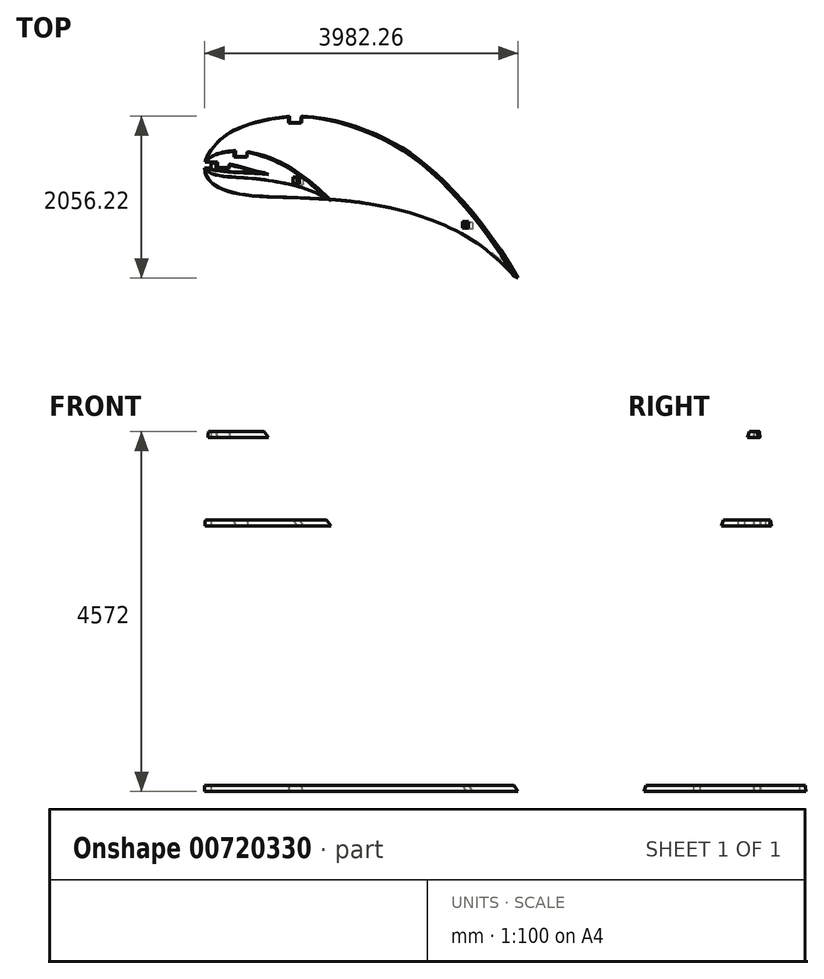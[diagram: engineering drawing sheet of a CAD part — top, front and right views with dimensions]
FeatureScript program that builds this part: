
annotation { "Feature Type Name" : "Feature", "Feature Type Description" : "" }
export const myFeature = defineFeature(function(context is Context, id is Id, definition is map)
    precondition{}
    {
        {
            var Q0;
            Q0=qCreatedBy(makeId("Top.planeOp"),FACE);
            var sketch = newSketch(context, id + "F0", { "sketchPlane" : qUnion([Q0])});
            skLineSegment(sketch, "E0", {"start": v(3981.78, -1434.37) * mm, "end": v(3974.28, -1438.04) * mm});
            skLineSegment(sketch, "E1", {"start": v(85.7, 203.58) * mm, "end": v(135.9, 258.57) * mm});
            skLineSegment(sketch, "E2", {"start": v(135.9, 258.57) * mm, "end": v(200.06, 322.02) * mm});
            skLineSegment(sketch, "E3", {"start": v(200.06, 322.02) * mm, "end": v(244.9, 359.43) * mm});
            skLineSegment(sketch, "E4", {"start": v(244.9, 359.43) * mm, "end": v(305.72, 402.46) * mm});
            skLineSegment(sketch, "E5", {"start": v(305.72, 402.46) * mm, "end": v(355.25, 432.28) * mm});
            skLineSegment(sketch, "E6", {"start": v(355.25, 432.28) * mm, "end": v(436.54, 473.24) * mm});
            skLineSegment(sketch, "E7", {"start": v(436.54, 473.24) * mm, "end": v(505.1, 502.14) * mm});
            skLineSegment(sketch, "E8", {"start": v(505.1, 502.14) * mm, "end": v(547.2, 518.05) * mm});
            skLineSegment(sketch, "E9", {"start": v(547.2, 518.05) * mm, "end": v(645.75, 551) * mm});
            skLineSegment(sketch, "E10", {"start": v(645.75, 551) * mm, "end": v(717.41, 570.86) * mm});
            skLineSegment(sketch, "E11", {"start": v(717.41, 570.86) * mm, "end": v(771.82, 583.4) * mm});
            skLineSegment(sketch, "E12", {"start": v(771.82, 583.4) * mm, "end": v(863.17, 599.45) * mm});
            skLineSegment(sketch, "E13", {"start": v(863.17, 599.45) * mm, "end": v(936.99, 608.65) * mm});
            skLineSegment(sketch, "E14", {"start": v(936.99, 608.65) * mm, "end": v(1020.95, 616.06) * mm});
            skLineSegment(sketch, "E15", {"start": v(1020.95, 616.06) * mm, "end": v(1085.5, 620.05) * mm});
            skLineSegment(sketch, "E16", {"start": v(1085.5, 620.05) * mm, "end": v(1159.87, 622.58) * mm});
            skLineSegment(sketch, "E17", {"start": v(1159.87, 622.58) * mm, "end": v(1234.2, 622.4) * mm});
            skLineSegment(sketch, "E18", {"start": v(1234.2, 622.4) * mm, "end": v(1290.49, 620.15) * mm});
            skLineSegment(sketch, "E19", {"start": v(1290.49, 620.15) * mm, "end": v(1382.4, 612.24) * mm});
            skLineSegment(sketch, "E20", {"start": v(1382.4, 612.24) * mm, "end": v(1456.14, 602.55) * mm});
            skLineSegment(sketch, "E21", {"start": v(1456.14, 602.55) * mm, "end": v(1568.2, 583.4) * mm});
            skLineSegment(sketch, "E22", {"start": v(1568.2, 583.4) * mm, "end": v(1675.53, 561.12) * mm});
            skLineSegment(sketch, "E23", {"start": v(1675.53, 561.12) * mm, "end": v(1747.83, 543.74) * mm});
            skLineSegment(sketch, "E24", {"start": v(1747.83, 543.74) * mm, "end": v(1854.08, 513.96) * mm});
            skLineSegment(sketch, "E25", {"start": v(1854.08, 513.96) * mm, "end": v(1890.59, 502.41) * mm});
            skLineSegment(sketch, "E26", {"start": v(1890.59, 502.41) * mm, "end": v(1960.9, 478.23) * mm});
            skLineSegment(sketch, "E27", {"start": v(1960.9, 478.23) * mm, "end": v(2030.46, 451.9) * mm});
            skLineSegment(sketch, "E28", {"start": v(2030.46, 451.9) * mm, "end": v(2135.88, 407.78) * mm});
            skLineSegment(sketch, "E29", {"start": v(2135.88, 407.78) * mm, "end": v(2301.28, 329.05) * mm});
            skLineSegment(sketch, "E30", {"start": v(2301.28, 329.05) * mm, "end": v(2413.59, 268.92) * mm});
            skLineSegment(sketch, "E31", {"start": v(2413.59, 268.92) * mm, "end": v(2559.73, 181.9) * mm});
            skLineSegment(sketch, "E32", {"start": v(2559.73, 181.9) * mm, "end": v(2621.95, 141.18) * mm});
            skLineSegment(sketch, "E33", {"start": v(2621.95, 141.18) * mm, "end": v(2679.05, 101.48) * mm});
            skLineSegment(sketch, "E34", {"start": v(2679.05, 101.48) * mm, "end": v(2742.61, 54.39) * mm});
            skLineSegment(sketch, "E35", {"start": v(2742.61, 54.39) * mm, "end": v(2801.11, 8.5) * mm});
            skLineSegment(sketch, "E36", {"start": v(2801.11, 8.5) * mm, "end": v(2924.09, -94.55) * mm});
            skLineSegment(sketch, "E37", {"start": v(2924.09, -94.55) * mm, "end": v(3026.4, -185.7) * mm});
            skLineSegment(sketch, "E38", {"start": v(3026.4, -185.7) * mm, "end": v(3152.8, -306.92) * mm});
            skLineSegment(sketch, "E39", {"start": v(3152.8, -306.92) * mm, "end": v(3237.33, -395.2) * mm});
            skLineSegment(sketch, "E40", {"start": v(3237.33, -395.2) * mm, "end": v(3357, -531.54) * mm});
            skLineSegment(sketch, "E41", {"start": v(3357, -531.54) * mm, "end": v(3429.97, -621.6) * mm});
            skLineSegment(sketch, "E42", {"start": v(3429.97, -621.6) * mm, "end": v(3532.6, -756.16) * mm});
            skLineSegment(sketch, "E43", {"start": v(3532.6, -756.16) * mm, "end": v(3608.12, -860.03) * mm});
            skLineSegment(sketch, "E44", {"start": v(3608.12, -860.03) * mm, "end": v(3683.71, -968.53) * mm});
            skLineSegment(sketch, "E45", {"start": v(3683.71, -968.53) * mm, "end": v(3810.32, -1164.56) * mm});
            skLineSegment(sketch, "E46", {"start": v(3810.32, -1164.56) * mm, "end": v(3852.67, -1234.8) * mm});
            skLineSegment(sketch, "E47", {"start": v(3852.67, -1234.8) * mm, "end": v(3904.25, -1315.67) * mm});
            skLineSegment(sketch, "E48", {"start": v(3904.25, -1315.67) * mm, "end": v(3931.4, -1354.4) * mm});
            skLineSegment(sketch, "E49", {"start": v(3931.4, -1354.4) * mm, "end": v(3951.82, -1385.8) * mm});
            skLineSegment(sketch, "E50", {"start": v(3951.82, -1385.8) * mm, "end": v(3965.5, -1409.6) * mm});
            skLineSegment(sketch, "E51", {"start": v(3965.5, -1409.6) * mm, "end": v(3976.53, -1431.19) * mm});
            skLineSegment(sketch, "E52", {"start": v(3976.53, -1431.19) * mm, "end": v(3977.76, -1434.1) * mm});
            skLineSegment(sketch, "E53", {"start": v(3977.76, -1434.1) * mm, "end": v(3977.52, -1436.02) * mm});
            skLineSegment(sketch, "E54", {"start": v(3977.52, -1436.02) * mm, "end": v(3974.68, -1432.88) * mm});
            skLineSegment(sketch, "E55", {"start": v(3974.68, -1432.88) * mm, "end": v(3970.05, -1426.8) * mm});
            skLineSegment(sketch, "E56", {"start": v(3970.05, -1426.8) * mm, "end": v(3963.95, -1418.37) * mm});
            skLineSegment(sketch, "E57", {"start": v(3963.95, -1418.37) * mm, "end": v(3948.7, -1396.74) * mm});
            skLineSegment(sketch, "E58", {"start": v(3948.7, -1396.74) * mm, "end": v(3928.75, -1368.76) * mm});
            skLineSegment(sketch, "E59", {"start": v(3928.75, -1368.76) * mm, "end": v(3899.46, -1330.66) * mm});
            skLineSegment(sketch, "E60", {"start": v(3899.46, -1330.66) * mm, "end": v(3884.92, -1313.42) * mm});
            skLineSegment(sketch, "E61", {"start": v(3884.92, -1313.42) * mm, "end": v(3871.19, -1298.28) * mm});
            skLineSegment(sketch, "E62", {"start": v(3871.19, -1298.28) * mm, "end": v(3858.13, -1284.94) * mm});
            skLineSegment(sketch, "E63", {"start": v(3858.13, -1284.94) * mm, "end": v(3833.49, -1262.37) * mm});
            skLineSegment(sketch, "E64", {"start": v(3833.49, -1262.37) * mm, "end": v(3781.73, -1221.74) * mm});
            skLineSegment(sketch, "E65", {"start": v(3781.73, -1221.74) * mm, "end": v(3761.1, -1205.6) * mm});
            skLineSegment(sketch, "E66", {"start": v(3761.1, -1205.6) * mm, "end": v(3734.78, -1184.46) * mm});
            skLineSegment(sketch, "E67", {"start": v(3734.78, -1184.46) * mm, "end": v(3678.72, -1138.45) * mm});
            skLineSegment(sketch, "E68", {"start": v(3678.72, -1138.45) * mm, "end": v(3619.1, -1089.72) * mm});
            skLineSegment(sketch, "E69", {"start": v(3619.1, -1089.72) * mm, "end": v(3557.15, -1040.93) * mm});
            skLineSegment(sketch, "E70", {"start": v(3557.15, -1040.93) * mm, "end": v(3520.35, -1013.45) * mm});
            skLineSegment(sketch, "E71", {"start": v(3520.35, -1013.45) * mm, "end": v(3430.66, -952.45) * mm});
            skLineSegment(sketch, "E72", {"start": v(3430.66, -952.45) * mm, "end": v(3366.7, -913.62) * mm});
            skLineSegment(sketch, "E73", {"start": v(3366.7, -913.62) * mm, "end": v(3302.14, -877.73) * mm});
            skLineSegment(sketch, "E74", {"start": v(3302.14, -877.73) * mm, "end": v(3236.86, -844.26) * mm});
            skLineSegment(sketch, "E75", {"start": v(3236.86, -844.26) * mm, "end": v(3136.46, -797) * mm});
            skLineSegment(sketch, "E76", {"start": v(3136.46, -797) * mm, "end": v(2967.04, -725.45) * mm});
            skLineSegment(sketch, "E77", {"start": v(2967.04, -725.45) * mm, "end": v(2827.36, -673.38) * mm});
            skLineSegment(sketch, "E78", {"start": v(2827.36, -673.38) * mm, "end": v(2654.54, -617.3) * mm});
            skLineSegment(sketch, "E79", {"start": v(2654.54, -617.3) * mm, "end": v(2542.14, -585.7) * mm});
            skLineSegment(sketch, "E80", {"start": v(2542.14, -585.7) * mm, "end": v(2397.64, -550.34) * mm});
            skLineSegment(sketch, "E81", {"start": v(2397.64, -550.34) * mm, "end": v(2252.1, -520.13) * mm});
            skLineSegment(sketch, "E82", {"start": v(2252.1, -520.13) * mm, "end": v(2131.8, -498.87) * mm});
            skLineSegment(sketch, "E83", {"start": v(2131.8, -498.87) * mm, "end": v(1958.49, -473.58) * mm});
            skLineSegment(sketch, "E84", {"start": v(1958.49, -473.58) * mm, "end": v(1810.72, -456.68) * mm});
            skLineSegment(sketch, "E85", {"start": v(1810.72, -456.68) * mm, "end": v(1633.55, -441.7) * mm});
            skLineSegment(sketch, "E86", {"start": v(1633.55, -441.7) * mm, "end": v(1514.16, -434.54) * mm});
            skLineSegment(sketch, "E87", {"start": v(1514.16, -434.54) * mm, "end": v(1365.64, -427.92) * mm});
            skLineSegment(sketch, "E88", {"start": v(1365.64, -427.92) * mm, "end": v(1184.3, -421.27) * mm});
            skLineSegment(sketch, "E89", {"start": v(1184.3, -421.27) * mm, "end": v(808.58, -404.94) * mm});
            skLineSegment(sketch, "E90", {"start": v(808.58, -404.94) * mm, "end": v(623.2, -392.8) * mm});
            skLineSegment(sketch, "E91", {"start": v(623.2, -392.8) * mm, "end": v(549.21, -385.3) * mm});
            skLineSegment(sketch, "E92", {"start": v(549.21, -385.3) * mm, "end": v(510.45, -380.43) * mm});
            skLineSegment(sketch, "E93", {"start": v(510.45, -380.43) * mm, "end": v(402.1, -362.18) * mm});
            skLineSegment(sketch, "E94", {"start": v(402.1, -362.18) * mm, "end": v(329.77, -344.76) * mm});
            skLineSegment(sketch, "E95", {"start": v(329.77, -344.76) * mm, "end": v(285.83, -331.42) * mm});
            skLineSegment(sketch, "E96", {"start": v(285.83, -331.42) * mm, "end": v(224.46, -308.34) * mm});
            skLineSegment(sketch, "E97", {"start": v(224.46, -308.34) * mm, "end": v(190.7, -292.72) * mm});
            skLineSegment(sketch, "E98", {"start": v(190.7, -292.72) * mm, "end": v(157.86, -274.98) * mm});
            skLineSegment(sketch, "E99", {"start": v(157.86, -274.98) * mm, "end": v(130.63, -257.91) * mm});
            skLineSegment(sketch, "E100", {"start": v(130.63, -257.91) * mm, "end": v(95.96, -232.16) * mm});
            skLineSegment(sketch, "E101", {"start": v(95.96, -232.16) * mm, "end": v(68.35, -206.64) * mm});
            skLineSegment(sketch, "E102", {"start": v(68.35, -206.64) * mm, "end": v(44.44, -178.1) * mm});
            skLineSegment(sketch, "E103", {"start": v(44.44, -178.1) * mm, "end": v(32.62, -159.9) * mm});
            skLineSegment(sketch, "E104", {"start": v(32.62, -159.9) * mm, "end": v(11.66, -111.7) * mm});
            skLineSegment(sketch, "E105", {"start": v(11.66, -111.7) * mm, "end": v(3.04, -75.1) * mm});
            skLineSegment(sketch, "E106", {"start": v(3.04, -75.1) * mm, "end": v(-0.05, -49.63) * mm});
            skLineSegment(sketch, "E107", {"start": v(-0.05, -49.63) * mm, "end": v(0, 0) * mm});
            skLineSegment(sketch, "E108", {"start": v(0, 0) * mm, "end": v(5.25, 37.05) * mm});
            skLineSegment(sketch, "E109", {"start": v(5.25, 37.05) * mm, "end": v(16.28, 76.98) * mm});
            skLineSegment(sketch, "E110", {"start": v(16.28, 76.98) * mm, "end": v(28.73, 107.24) * mm});
            skLineSegment(sketch, "E111", {"start": v(28.73, 107.24) * mm, "end": v(45.88, 140.13) * mm});
            skLineSegment(sketch, "E112", {"start": v(45.88, 140.13) * mm, "end": v(85.7, 203.58) * mm});
            skSolve(sketch);
        }
        {
            var Q0;
            Q0=qCreatedBy(makeId("Top.planeOp"),FACE);
            var sketch = newSketch(context, id + "F1", { "sketchPlane" : qUnion([Q0])});
            skPoint(sketch, "E113", {"position": v(0, 0) * mm});
            skPoint(sketch, "E114.0", {"position": v(-0.05, -49.63) * mm});
            skPoint(sketch, "E114.1", {"position": v(11.66, -111.7) * mm});
            skPoint(sketch, "E114.2", {"position": v(68.35, -206.64) * mm});
            skPoint(sketch, "E114.3", {"position": v(5.25, 37.05) * mm});
            skPoint(sketch, "E114.4", {"position": v(28.73, 107.24) * mm});
            skPoint(sketch, "E114.5", {"position": v(135.9, 258.57) * mm});
            skPoint(sketch, "E114.6", {"position": v(355.25, 432.28) * mm});
            skPoint(sketch, "E114.7", {"position": v(1159.87, 622.58) * mm});
            skPoint(sketch, "E114.8", {"position": v(2135.88, 407.78) * mm});
            skPoint(sketch, "E114.9", {"position": v(3981.78, -1434.37) * mm});
            skPoint(sketch, "E114.10", {"position": v(2967.04, -725.45) * mm});
            skPoint(sketch, "E114.11", {"position": v(1810.72, -456.68) * mm});
            skPoint(sketch, "E114.12", {"position": v(808.58, -404.94) * mm});
            skPoint(sketch, "E114.13", {"position": v(285.83, -331.42) * mm});
            skPoint(sketch, "E114.14", {"position": v(2862.6, -43.02) * mm});
            skFitSpline(sketch, "E115", {"points": [v(0, 0) * mm, v(-0.05, -49.63) * mm, v(11.66, -111.7) * mm, v(68.35, -206.64) * mm, v(285.83, -331.42) * mm, v(808.58, -404.94) * mm, v(1810.72, -456.68) * mm, v(2967.04, -725.45) * mm, v(3981.78, -1434.37) * mm], "startDerivative": vector(-39.2, -1147.22) * mm, "endDerivative": vector(4484.15, -5091.63) * mm});
            skFitSpline(sketch, "E116", {"points": [v(0, 0) * mm, v(5.25, 37.05) * mm, v(28.73, 107.24) * mm, v(135.9, 258.57) * mm, v(355.25, 432.28) * mm, v(1159.87, 622.58) * mm, v(2135.88, 407.78) * mm, v(2862.6, -43.02) * mm, v(3981.78, -1434.37) * mm], "startDerivative": vector(115.79, 1014.55) * mm, "endDerivative": vector(4272.99, -7495.32) * mm});
            skSolve(sketch);
        }
        {
            var Q0;
            Q0=qCreatedBy(makeId("Top.planeOp"),FACE);
            cPlane(context, id + "F2", {"entities" : qUnion([Q0]), "cplaneType" : CPlaneType.OFFSET, "offset" : 4572 * mm, "width" : 152.4 * mm, "height" : 152.4 * mm});
        }
        {
            var Q0;
            Q0=qCreatedBy(id+"F2.planeOp",FACE);
            var sketch = newSketch(context, id + "F3", { "sketchPlane" : qUnion([Q0])});
            skLineSegment(sketch, "E117", {"start": v(0, 0) * mm, "end": v(2.44, 5.76) * mm});
            skLineSegment(sketch, "E118", {"start": v(2.44, 5.76) * mm, "end": v(3.9, 8.43) * mm});
            skLineSegment(sketch, "E119", {"start": v(3.9, 8.43) * mm, "end": v(6.05, 11.35) * mm});
            skLineSegment(sketch, "E120", {"start": v(6.05, 11.35) * mm, "end": v(7.68, 12.92) * mm});
            skLineSegment(sketch, "E121", {"start": v(7.68, 12.92) * mm, "end": v(10.08, 14.68) * mm});
            skLineSegment(sketch, "E122", {"start": v(10.08, 14.68) * mm, "end": v(15.58, 17.45) * mm});
            skLineSegment(sketch, "E123", {"start": v(15.58, 17.45) * mm, "end": v(21.94, 19.67) * mm});
            skLineSegment(sketch, "E124", {"start": v(21.94, 19.67) * mm, "end": v(39.32, 24.27) * mm});
            skLineSegment(sketch, "E125", {"start": v(39.32, 24.27) * mm, "end": v(46.9, 25.72) * mm});
            skLineSegment(sketch, "E126", {"start": v(46.9, 25.72) * mm, "end": v(63.21, 27.76) * mm});
            skLineSegment(sketch, "E127", {"start": v(63.21, 27.76) * mm, "end": v(80.93, 28.74) * mm});
            skLineSegment(sketch, "E128", {"start": v(80.93, 28.74) * mm, "end": v(87.62, 28.87) * mm});
            skLineSegment(sketch, "E129", {"start": v(87.62, 28.87) * mm, "end": v(123.3, 27.99) * mm});
            skLineSegment(sketch, "E130", {"start": v(123.3, 27.99) * mm, "end": v(136.22, 27.24) * mm});
            skLineSegment(sketch, "E131", {"start": v(136.22, 27.24) * mm, "end": v(172.46, 24.2) * mm});
            skLineSegment(sketch, "E132", {"start": v(172.46, 24.2) * mm, "end": v(184.68, 22.84) * mm});
            skLineSegment(sketch, "E133", {"start": v(184.68, 22.84) * mm, "end": v(208.8, 19.63) * mm});
            skLineSegment(sketch, "E134", {"start": v(208.8, 19.63) * mm, "end": v(227.68, 16.64) * mm});
            skLineSegment(sketch, "E135", {"start": v(227.68, 16.64) * mm, "end": v(287.43, 5.3) * mm});
            skLineSegment(sketch, "E136", {"start": v(287.43, 5.3) * mm, "end": v(328.35, -2.8) * mm});
            skLineSegment(sketch, "E137", {"start": v(328.35, -2.8) * mm, "end": v(350.97, -7.56) * mm});
            skLineSegment(sketch, "E138", {"start": v(350.97, -7.56) * mm, "end": v(375.86, -13.24) * mm});
            skLineSegment(sketch, "E139", {"start": v(375.86, -13.24) * mm, "end": v(415.26, -22.7) * mm});
            skLineSegment(sketch, "E140", {"start": v(415.26, -22.7) * mm, "end": v(480.32, -37.82) * mm});
            skLineSegment(sketch, "E141", {"start": v(480.32, -37.82) * mm, "end": v(518.03, -46.34) * mm});
            skLineSegment(sketch, "E142", {"start": v(518.03, -46.34) * mm, "end": v(543.1, -52.2) * mm});
            skLineSegment(sketch, "E143", {"start": v(543.1, -52.2) * mm, "end": v(601.34, -66.56) * mm});
            skLineSegment(sketch, "E144", {"start": v(601.34, -66.56) * mm, "end": v(636.38, -74.84) * mm});
            skLineSegment(sketch, "E145", {"start": v(636.38, -74.84) * mm, "end": v(653.53, -78.67) * mm});
            skLineSegment(sketch, "E146", {"start": v(653.53, -78.67) * mm, "end": v(683.57, -85.02) * mm});
            skLineSegment(sketch, "E147", {"start": v(683.57, -85.02) * mm, "end": v(696.65, -87.74) * mm});
            skLineSegment(sketch, "E148", {"start": v(696.65, -87.74) * mm, "end": v(720.28, -92.43) * mm});
            skLineSegment(sketch, "E149", {"start": v(720.28, -92.43) * mm, "end": v(725.98, -93.35) * mm});
            skLineSegment(sketch, "E150", {"start": v(725.98, -93.35) * mm, "end": v(729.17, -93.8) * mm});
            skLineSegment(sketch, "E151", {"start": v(729.17, -93.8) * mm, "end": v(736.55, -94.66) * mm});
            skLineSegment(sketch, "E152", {"start": v(736.55, -94.66) * mm, "end": v(742.43, -95.48) * mm});
            skLineSegment(sketch, "E153", {"start": v(742.43, -95.48) * mm, "end": v(745.85, -96.07) * mm});
            skLineSegment(sketch, "E154", {"start": v(745.85, -96.07) * mm, "end": v(749.6, -96.82) * mm});
            skLineSegment(sketch, "E155", {"start": v(749.6, -96.82) * mm, "end": v(753.66, -97.74) * mm});
            skLineSegment(sketch, "E156", {"start": v(753.66, -97.74) * mm, "end": v(755.05, -98.1) * mm});
            skLineSegment(sketch, "E157", {"start": v(755.05, -98.1) * mm, "end": v(755.65, -98.33) * mm});
            skLineSegment(sketch, "E158", {"start": v(755.65, -98.33) * mm, "end": v(755.22, -98.36) * mm});
            skLineSegment(sketch, "E159", {"start": v(755.22, -98.36) * mm, "end": v(753.96, -98.24) * mm});
            skLineSegment(sketch, "E160", {"start": v(753.96, -98.24) * mm, "end": v(748.84, -97.58) * mm});
            skLineSegment(sketch, "E161", {"start": v(748.84, -97.58) * mm, "end": v(745.9, -97.19) * mm});
            skLineSegment(sketch, "E162", {"start": v(745.9, -97.19) * mm, "end": v(742.3, -96.73) * mm});
            skLineSegment(sketch, "E163", {"start": v(742.3, -96.73) * mm, "end": v(739.1, -96.35) * mm});
            skLineSegment(sketch, "E164", {"start": v(739.1, -96.35) * mm, "end": v(736.2, -96.03) * mm});
            skLineSegment(sketch, "E165", {"start": v(736.2, -96.03) * mm, "end": v(730.95, -95.55) * mm});
            skLineSegment(sketch, "E166", {"start": v(730.95, -95.55) * mm, "end": v(727.66, -95.3) * mm});
            skLineSegment(sketch, "E167", {"start": v(727.66, -95.3) * mm, "end": v(720.08, -94.85) * mm});
            skLineSegment(sketch, "E168", {"start": v(720.08, -94.85) * mm, "end": v(707.85, -94.3) * mm});
            skLineSegment(sketch, "E169", {"start": v(707.85, -94.3) * mm, "end": v(694.38, -93.8) * mm});
            skLineSegment(sketch, "E170", {"start": v(694.38, -93.8) * mm, "end": v(649.75, -92.28) * mm});
            skLineSegment(sketch, "E171", {"start": v(649.75, -92.28) * mm, "end": v(596.8, -90.77) * mm});
            skLineSegment(sketch, "E172", {"start": v(596.8, -90.77) * mm, "end": v(537.05, -90.01) * mm});
            skLineSegment(sketch, "E173", {"start": v(537.05, -90.01) * mm, "end": v(512.7, -89.51) * mm});
            skLineSegment(sketch, "E174", {"start": v(512.7, -89.51) * mm, "end": v(472.75, -88.5) * mm});
            skLineSegment(sketch, "E175", {"start": v(472.75, -88.5) * mm, "end": v(406.19, -86.99) * mm});
            skLineSegment(sketch, "E176", {"start": v(406.19, -86.99) * mm, "end": v(366.78, -85.77) * mm});
            skLineSegment(sketch, "E177", {"start": v(366.78, -85.77) * mm, "end": v(341.14, -84.72) * mm});
            skLineSegment(sketch, "E178", {"start": v(341.14, -84.72) * mm, "end": v(276.84, -80.93) * mm});
            skLineSegment(sketch, "E179", {"start": v(276.84, -80.93) * mm, "end": v(245.36, -78.48) * mm});
            skLineSegment(sketch, "E180", {"start": v(245.36, -78.48) * mm, "end": v(216.33, -75.64) * mm});
            skLineSegment(sketch, "E181", {"start": v(216.33, -75.64) * mm, "end": v(196.98, -73.34) * mm});
            skLineSegment(sketch, "E182", {"start": v(196.98, -73.34) * mm, "end": v(161.11, -68.08) * mm});
            skLineSegment(sketch, "E183", {"start": v(161.11, -68.08) * mm, "end": v(148.89, -65.97) * mm});
            skLineSegment(sketch, "E184", {"start": v(148.89, -65.97) * mm, "end": v(124.98, -61.47) * mm});
            skLineSegment(sketch, "E185", {"start": v(124.98, -61.47) * mm, "end": v(112.7, -59) * mm});
            skLineSegment(sketch, "E186", {"start": v(112.7, -59) * mm, "end": v(89.3, -53.87) * mm});
            skLineSegment(sketch, "E187", {"start": v(89.3, -53.87) * mm, "end": v(71.86, -49.17) * mm});
            skLineSegment(sketch, "E188", {"start": v(71.86, -49.17) * mm, "end": v(65.84, -47.26) * mm});
            skLineSegment(sketch, "E189", {"start": v(65.84, -47.26) * mm, "end": v(54.33, -43.15) * mm});
            skLineSegment(sketch, "E190", {"start": v(54.33, -43.15) * mm, "end": v(40.09, -37.06) * mm});
            skLineSegment(sketch, "E191", {"start": v(40.09, -37.06) * mm, "end": v(32.34, -33.2) * mm});
            skLineSegment(sketch, "E192", {"start": v(32.34, -33.2) * mm, "end": v(16.64, -24.2) * mm});
            skLineSegment(sketch, "E193", {"start": v(16.64, -24.2) * mm, "end": v(11.09, -20.57) * mm});
            skLineSegment(sketch, "E194", {"start": v(11.09, -20.57) * mm, "end": v(6.37, -16.6) * mm});
            skLineSegment(sketch, "E195", {"start": v(6.37, -16.6) * mm, "end": v(4.43, -14.33) * mm});
            skLineSegment(sketch, "E196", {"start": v(4.43, -14.33) * mm, "end": v(3.03, -12.1) * mm});
            skLineSegment(sketch, "E197", {"start": v(3.03, -12.1) * mm, "end": v(1.77, -9.1) * mm});
            skLineSegment(sketch, "E198", {"start": v(1.77, -9.1) * mm, "end": v(1, -6.17) * mm});
            skLineSegment(sketch, "E199", {"start": v(1, -6.17) * mm, "end": v(0, 0) * mm});
            skSolve(sketch);
        }
        {
            var Q0;
            Q0=qCreatedBy(id+"F2.planeOp",FACE);
            var sketch = newSketch(context, id + "F4", { "sketchPlane" : qUnion([Q0])});
            skPoint(sketch, "E200.0", {"position": v(2.44, 5.76) * mm});
            skPoint(sketch, "E201.0", {"position": v(0, 0) * mm});
            skPoint(sketch, "E202.0", {"position": v(1, -6.17) * mm});
            skPoint(sketch, "E203.0", {"position": v(5.4, -15.46) * mm});
            skPoint(sketch, "E204.0", {"position": v(16.64, -24.2) * mm});
            skPoint(sketch, "E205.0", {"position": v(40.09, -37.06) * mm});
            skPoint(sketch, "E206.0", {"position": v(89.3, -53.87) * mm});
            skPoint(sketch, "E207.0", {"position": v(148.89, -65.97) * mm});
            skPoint(sketch, "E207.1", {"position": v(341.14, -84.72) * mm});
            skPoint(sketch, "E207.2", {"position": v(755.65, -98.33) * mm});
            skPoint(sketch, "E207.3", {"position": v(415.26, -22.7) * mm});
            skPoint(sketch, "E207.4", {"position": v(227.68, 16.64) * mm});
            skPoint(sketch, "E207.5", {"position": v(80.93, 28.74) * mm});
            skPoint(sketch, "E207.6", {"position": v(39.32, 24.27) * mm});
            skPoint(sketch, "E207.7", {"position": v(15.58, 17.45) * mm});
            skPoint(sketch, "E207.8", {"position": v(6.87, 12.13) * mm});
            skFitSpline(sketch, "E208", {"points": [v(0, 0) * mm, v(2.44, 5.76) * mm, v(6.87, 12.13) * mm, v(15.58, 17.45) * mm, v(39.32, 24.27) * mm, v(80.93, 28.74) * mm, v(227.68, 16.64) * mm, v(415.26, -22.7) * mm, v(755.65, -98.33) * mm], "startDerivative": vector(56.06, 146.59) * mm, "endDerivative": vector(1282.77, -261.85) * mm});
            skFitSpline(sketch, "E209", {"points": [v(0, 0) * mm, v(1, -6.17) * mm, v(5.4, -15.46) * mm, v(16.64, -24.2) * mm, v(40.09, -37.06) * mm, v(89.3, -53.87) * mm, v(148.89, -65.97) * mm, v(341.14, -84.72) * mm, v(755.65, -98.33) * mm], "startDerivative": vector(15.7, -149.12) * mm, "endDerivative": vector(1341.07, -77.84) * mm});
            skSolve(sketch);
        }
        {
            var Q0;
            Q0=makeQuery(id+"F1.imprint","IMPRINT",FACE,{"disambiguationData":[TD([[makeQuery(id+"F1.imprint","IMPRINT",EDGE,{"derivedFrom":sQuery(id+"F1.wireOp",EDGE,"E115")}),1.0]])]});
            var Q1;
            Q1=makeQuery(id+"F4.imprint","IMPRINT",FACE,{"disambiguationData":[TD([[makeQuery(id+"F4.imprint","IMPRINT",EDGE,{"derivedFrom":sQuery(id+"F4.wireOp",EDGE,"E208")}),-1.0]])]});
            loft(context, id + "F5", {"sheetProfilesArray" : [{ "sheetProfileEntities" : qUnion([Q0]) }, { "sheetProfileEntities" : qUnion([Q1]) }]});
        }
        {
            var Q0;
            Q0=qCreatedBy(makeId("Front.planeOp"),FACE);
            var sketch = newSketch(context, id + "F6", { "sketchPlane" : qUnion([Q0])});
            skPoint(sketch, "E210", {"position": v(0, 0) * mm});
            skLineSegment(sketch, "E211", {"start": v(0, 0) * mm, "end": v(0, 76.2) * mm, "construction": true});
            skLineSegment(sketch, "E212.bottom", {"start": v(0, 76.2) * mm, "end": v(5797.2, 76.2) * mm});
            skLineSegment(sketch, "E212.top", {"start": v(0, 1123.95) * mm, "end": v(5797.2, 1123.95) * mm});
            skLineSegment(sketch, "E212.left", {"start": v(0, 76.2) * mm, "end": v(0, 1123.95) * mm});
            skLineSegment(sketch, "E212.right", {"start": v(5797.2, 76.2) * mm, "end": v(5797.2, 1123.95) * mm});
            skLineSegment(sketch, "E213.0.1.0", {"start": v(0, 1200.15) * mm, "end": v(5797.2, 1200.15) * mm});
            skLineSegment(sketch, "E213.0.1.1", {"start": v(0, 2247.9) * mm, "end": v(5797.2, 2247.9) * mm});
            skLineSegment(sketch, "E213.0.1.2", {"start": v(0, 1200.15) * mm, "end": v(0, 2247.9) * mm});
            skLineSegment(sketch, "E213.0.1.3", {"start": v(5797.2, 1200.15) * mm, "end": v(5797.2, 2247.9) * mm});
            skPoint(sketch, "E213.0.1.4", {"position": v(0, 1123.95) * mm});
            skLineSegment(sketch, "E213.0.1.5", {"start": v(0, 1123.95) * mm, "end": v(0, 1200.15) * mm, "construction": true});
            skLineSegment(sketch, "E213.0.2.0", {"start": v(0, 2324.1) * mm, "end": v(5797.2, 2324.1) * mm});
            skLineSegment(sketch, "E213.0.2.1", {"start": v(0, 3371.85) * mm, "end": v(5797.2, 3371.85) * mm});
            skLineSegment(sketch, "E213.0.2.2", {"start": v(0, 2324.1) * mm, "end": v(0, 3371.85) * mm});
            skLineSegment(sketch, "E213.0.2.3", {"start": v(5797.2, 2324.1) * mm, "end": v(5797.2, 3371.85) * mm});
            skPoint(sketch, "E213.0.2.4", {"position": v(0, 2247.9) * mm});
            skLineSegment(sketch, "E213.0.2.5", {"start": v(0, 2247.9) * mm, "end": v(0, 2324.1) * mm, "construction": true});
            skLineSegment(sketch, "E213.0.3.0", {"start": v(0, 3448.05) * mm, "end": v(5797.2, 3448.05) * mm});
            skLineSegment(sketch, "E213.0.3.1", {"start": v(0, 4495.8) * mm, "end": v(5797.2, 4495.8) * mm});
            skLineSegment(sketch, "E213.0.3.2", {"start": v(0, 3448.05) * mm, "end": v(0, 4495.8) * mm});
            skLineSegment(sketch, "E213.0.3.3", {"start": v(5797.2, 3448.05) * mm, "end": v(5797.2, 4495.8) * mm});
            skPoint(sketch, "E213.0.3.4", {"position": v(0, 3371.85) * mm});
            skLineSegment(sketch, "E213.0.3.5", {"start": v(0, 3371.85) * mm, "end": v(0, 3448.05) * mm, "construction": true});
            skLineSegment(sketch, "E213.direction1", {"start": v(0, 0) * mm, "end": v(25.4, 0) * mm, "construction": true});
            skLineSegment(sketch, "E213.direction2", {"start": v(0, 0) * mm, "end": v(0, 1123.95) * mm, "construction": true});
            skSolve(sketch);
        }
        {
            var Q0;
            Q0=makeQuery(id+"F6.imprint","IMPRINT",FACE,{"disambiguationData":[TD([[makeQuery(id+"F6.imprint","IMPRINT",EDGE,{"derivedFrom":sQuery(id+"F6.wireOp",EDGE,"E213.0.3.0")}),1.0]])]});
            var Q1;
            Q1=makeQuery(id+"F6.imprint","IMPRINT",FACE,{"disambiguationData":[TD([[makeQuery(id+"F6.imprint","IMPRINT",EDGE,{"derivedFrom":sQuery(id+"F6.wireOp",EDGE,"E213.0.2.0")}),1.0]])]});
            var Q2;
            Q2=makeQuery(id+"F6.imprint","IMPRINT",FACE,{"disambiguationData":[TD([[makeQuery(id+"F6.imprint","IMPRINT",EDGE,{"derivedFrom":sQuery(id+"F6.wireOp",EDGE,"E213.0.1.0")}),1.0]])]});
            var Q3;
            Q3=makeQuery(id+"F6.imprint","IMPRINT",FACE,{"disambiguationData":[TD([[makeQuery(id+"F6.imprint","IMPRINT",EDGE,{"derivedFrom":sQuery(id+"F6.wireOp",EDGE,"E212.bottom")}),1.0]])]});
            extrude(context, id + "F7", {"entities" : qUnion([Q0, Q1, Q2, Q3]), "operationType" : NewBodyOperationType.REMOVE, "endBound" : BoundingType.SYMMETRIC, "oppositeDirection" : true, "depth" : 3556 * mm, "offsetDistance" : 25.4 * mm});
        }
        {
            var Q0;
            Q0=makeQuery(id+"F7.boolean.opBoolean","COPY",FACE,{"derivedFrom":makeQuery(id+"F7.opExtrude","SWEPT_FACE",FACE,{"disambiguationData":[OSD([sQuery(id+"F6.wireOp",EDGE,"E212.left")])]})});
            var Q1;
            Q1=makeQuery(id+"F7.boolean.opBoolean","COPY",FACE,{"derivedFrom":makeQuery(id+"F7.opExtrude","SWEPT_FACE",FACE,{"disambiguationData":[OSD([sQuery(id+"F6.wireOp",EDGE,"E213.0.1.2")])]})});
            var Q2;
            Q2=makeQuery(id+"F7.boolean.opBoolean","COPY",FACE,{"derivedFrom":makeQuery(id+"F7.opExtrude","SWEPT_FACE",FACE,{"disambiguationData":[OSD([sQuery(id+"F6.wireOp",EDGE,"E213.0.2.2")])]})});
            extrude(context, id + "F8", {"entities" : qUnion([Q0, Q1, Q2]), "operationType" : NewBodyOperationType.REMOVE, "oppositeDirection" : true, "depth" : 127 * mm, "offsetDistance" : 25.4 * mm});
        }
        {
            var Q0;
            Q0=qCreatedBy(makeId("Top.planeOp"),FACE);
            var sketch = newSketch(context, id + "F9", { "sketchPlane" : qUnion([Q0])});
            skPoint(sketch, "E214", {"position": v(0, 0) * mm});
            skLineSegment(sketch, "E215", {"start": v(0, 0) * mm, "end": v(80.65, 0) * mm, "construction": true});
            skLineSegment(sketch, "E216", {"start": v(80.65, 0) * mm, "end": v(80.65, 40.34) * mm});
            skLineSegment(sketch, "E217", {"start": v(80.65, 0) * mm, "end": v(80.65, -40.34) * mm});
            skLineSegment(sketch, "E218", {"start": v(80.65, -40.34) * mm, "end": v(0, -40.34) * mm});
            skLineSegment(sketch, "E219", {"start": v(80.65, 40.34) * mm, "end": v(0, 40.34) * mm});
            skLineSegment(sketch, "E220", {"start": v(0, 40.34) * mm, "end": v(0, -40.34) * mm});
            skSolve(sketch);
        }
        {
            var Q0;
            Q0=makeQuery(id+"F9.imprint","IMPRINT",FACE,{"disambiguationData":[TD([[makeQuery(id+"F9.imprint","IMPRINT",EDGE,{"derivedFrom":sQuery(id+"F9.wireOp",EDGE,"E216")}),1.0]])]});
            extrude(context, id + "F10", {"entities" : qUnion([Q0]), "operationType" : NewBodyOperationType.REMOVE, "depth" : 5080 * mm, "offsetDistance" : 25.4 * mm});
        }
        {
            var Q0;
            Q0=makeQuery(id+"F10.boolean.opBoolean","SPLIT",BODY,{"disambiguationData":[OD(0.0)],"derivedFrom":makeQuery(id+"F8.boolean.opBoolean","SPLIT",BODY,{"disambiguationData":[OD(1.0)],"derivedFrom":makeQuery(id+"F7.boolean.opBoolean","SPLIT",BODY,{"disambiguationData":[OD(2.0)],"derivedFrom":makeQuery(id+"F5.opLoft","SWEPT_BODY",BODY,{"disambiguationData":[OSD([makeQuery(id+"F1.imprint","IMPRINT",FACE,{"disambiguationData":[TD([[makeQuery(id+"F1.imprint","IMPRINT",EDGE,{"derivedFrom":sQuery(id+"F1.wireOp",EDGE,"E115")}),1.0]])]}),makeQuery(id+"F4.imprint","IMPRINT",FACE,{"disambiguationData":[TD([[makeQuery(id+"F4.imprint","IMPRINT",EDGE,{"derivedFrom":sQuery(id+"F4.wireOp",EDGE,"E208")}),-1.0]])]})])]})})})});
            var Q1;
            Q1=makeQuery(id+"F10.boolean.opBoolean","SPLIT",BODY,{"disambiguationData":[OD(0.0)],"derivedFrom":makeQuery(id+"F8.boolean.opBoolean","SPLIT",BODY,{"disambiguationData":[OD(2.0)],"derivedFrom":makeQuery(id+"F7.boolean.opBoolean","SPLIT",BODY,{"disambiguationData":[OD(2.0)],"derivedFrom":makeQuery(id+"F5.opLoft","SWEPT_BODY",BODY,{"disambiguationData":[OSD([makeQuery(id+"F1.imprint","IMPRINT",FACE,{"disambiguationData":[TD([[makeQuery(id+"F1.imprint","IMPRINT",EDGE,{"derivedFrom":sQuery(id+"F1.wireOp",EDGE,"E115")}),1.0]])]}),makeQuery(id+"F4.imprint","IMPRINT",FACE,{"disambiguationData":[TD([[makeQuery(id+"F4.imprint","IMPRINT",EDGE,{"derivedFrom":sQuery(id+"F4.wireOp",EDGE,"E208")}),-1.0]])]})])]})})})});
            deleteBodies(context, id + "F11", {"entities" : qUnion([Q0, Q1])});
        }
        {
            var Q0;
            {var subQ0=sQuery(id+"F6.wireOp",EDGE,"E212.bottom");Q0=makeQuery(id+"F10.boolean.opBoolean","COPY",FACE,{"disambiguationData":[TD([makeQuery(id+"F7.boolean.opBoolean","COPY",FACE,{"derivedFrom":makeQuery(id+"F7.opExtrude","SWEPT_FACE",FACE,{"disambiguationData":[OSD([subQ0])]})})])],"derivedFrom":makeQuery(id+"F10.opExtrude","SWEPT_FACE",FACE,{"disambiguationData":[OSD([sQuery(id+"F9.wireOp",EDGE,"E220")])]})});}
            extrude(context, id + "F12", {"entities" : qUnion([Q0]), "operationType" : NewBodyOperationType.REMOVE, "oppositeDirection" : true, "depth" : 25.4 * mm, "offsetDistance" : 25.4 * mm});
        }
        {
            var Q0;
            Q0=makeQuery(id+"F1.imprint","IMPRINT",FACE,{"disambiguationData":[TD([[makeQuery(id+"F1.imprint","IMPRINT",EDGE,{"derivedFrom":sQuery(id+"F1.wireOp",EDGE,"E115")}),1.0]])]});
            var sketch = newSketch(context, id + "F13", { "sketchPlane" : qUnion([Q0])});
            skPoint(sketch, "E221.0", {"position": v(1159.87, 622.58) * mm});
            skLineSegment(sketch, "E222", {"start": v(1159.87, 622.58) * mm, "end": v(1159.87, 541.93) * mm, "construction": true});
            skLineSegment(sketch, "E223", {"start": v(1159.87, 541.93) * mm, "end": v(1240.52, 541.93) * mm});
            skLineSegment(sketch, "E224", {"start": v(1159.87, 541.93) * mm, "end": v(1079.23, 541.93) * mm});
            skLineSegment(sketch, "E225", {"start": v(1079.23, 541.93) * mm, "end": v(1079.23, 622.58) * mm});
            skLineSegment(sketch, "E226", {"start": v(1079.23, 622.58) * mm, "end": v(1240.52, 622.58) * mm});
            skLineSegment(sketch, "E227", {"start": v(1240.52, 622.58) * mm, "end": v(1240.52, 541.93) * mm});
            skSolve(sketch);
        }
        {
            var Q0;
            Q0=makeQuery(id+"F5.opLoft","CAP_FACE",FACE,{"disambiguationData":[OSD([makeQuery(id+"F4.imprint","IMPRINT",FACE,{"disambiguationData":[TD([[makeQuery(id+"F4.imprint","IMPRINT",EDGE,{"derivedFrom":sQuery(id+"F4.wireOp",EDGE,"E208")}),-1.0]])]})])],"isStart":true});
            var sketch = newSketch(context, id + "F14", { "sketchPlane" : qUnion([Q0])});
            skFitSpline(sketch, "E228.0", {"points": [v(809.41, -120.6) * mm, v(779.44, -112) * mm, v(719.48, -94.8) * mm, v(644.5, -73.42) * mm, v(584.48, -56.48) * mm, v(539.43, -43.9) * mm, v(494.33, -31.47) * mm, v(456.7, -21.28) * mm, v(426.57, -13.24) * mm, v(403.94, -7.3) * mm, v(381.28, -1.5) * mm, v(358.59, 4.1) * mm, v(335.84, 9.44) * mm, v(313.03, 14.49) * mm, v(290.14, 19.15) * mm, v(267.15, 23.35) * mm, v(247.91, 26.43) * mm, v(232.46, 28.63) * mm, v(220.85, 30.15) * mm, v(209.2, 31.55) * mm, v(193.68, 33.23) * mm, v(174.24, 35) * mm, v(154.76, 36.3) * mm, v(139.15, 37.02) * mm, v(127.44, 37.39) * mm, v(115.73, 37.56) * mm, v(105.96, 37.52) * mm, v(98.15, 37.34) * mm, v(90.34, 37.06) * mm, v(84.51, 36.71) * mm, v(80.65, 36.4) * mm], "construction": true});
            skLineSegment(sketch, "E229", {"start": v(144.85, 36.75) * mm, "end": v(144.85, -43.9) * mm});
            skLineSegment(sketch, "E230", {"start": v(144.85, -43.9) * mm, "end": v(306.14, -43.9) * mm});
            skLineSegment(sketch, "E231", {"start": v(306.14, -43.9) * mm, "end": v(306.14, 36.75) * mm});
            skLineSegment(sketch, "E232", {"start": v(306.14, 36.75) * mm, "end": v(144.85, 36.75) * mm});
            skSolve(sketch);
        }
        {
            var Q0;
            {var subQ0=sQuery(id+"F14.wireOp",EDGE,"E230");Q0=makeQuery(id+"F14.imprint","IMPRINT",FACE,{"disambiguationData":[TD([[makeQuery(id+"F14.imprint","IMPRINT",EDGE,{"derivedFrom":subQ0}),1.0]])]});}
            cPlane(context, id + "F15", {"entities" : qUnion([Q0]), "cplaneType" : CPlaneType.OFFSET, "offset" : 0 * mm, "width" : 152.4 * mm, "height" : 152.4 * mm});
        }
        {
            var Q0;
            Q0=qCreatedBy(id+"F15.planeOp",FACE);
            var sketch = newSketch(context, id + "F16", { "sketchPlane" : qUnion([Q0])});
            skLineSegment(sketch, "E233.0", {"start": v(144.85, 36.75) * mm, "end": v(144.85, -43.9) * mm});
            skLineSegment(sketch, "E233.1", {"start": v(144.85, -43.9) * mm, "end": v(306.14, -43.9) * mm});
            skLineSegment(sketch, "E233.2", {"start": v(306.14, -43.9) * mm, "end": v(306.14, 36.75) * mm});
            skLineSegment(sketch, "E233.3", {"start": v(306.14, 36.75) * mm, "end": v(144.85, 36.75) * mm});
            skSolve(sketch);
        }
        {
            var Q0;
            Q0=makeQuery(id+"F1.imprint","IMPRINT",FACE,{"disambiguationData":[TD([[makeQuery(id+"F1.imprint","IMPRINT",EDGE,{"derivedFrom":sQuery(id+"F1.wireOp",EDGE,"E115")}),1.0]])]});
            cPlane(context, id + "F17", {"entities" : qUnion([Q0]), "cplaneType" : CPlaneType.OFFSET, "offset" : 0 * mm, "width" : 152.4 * mm, "height" : 152.4 * mm});
        }
        {
            var Q0;
            Q0=qCreatedBy(id+"F17.planeOp",FACE);
            var sketch = newSketch(context, id + "F18", { "sketchPlane" : qUnion([Q0])});
            skLineSegment(sketch, "E234.0", {"start": v(1240.52, 622.58) * mm, "end": v(1240.52, 541.93) * mm});
            skLineSegment(sketch, "E234.1", {"start": v(1079.23, 622.58) * mm, "end": v(1240.52, 622.58) * mm});
            skLineSegment(sketch, "E234.2", {"start": v(1079.23, 541.93) * mm, "end": v(1079.23, 622.58) * mm});
            skLineSegment(sketch, "E235", {"start": v(1240.52, 541.93) * mm, "end": v(1079.23, 541.93) * mm});
            skSolve(sketch);
        }
        {
            var Q0;
            Q0 = qSketchRegion(id + "F16", true);
            var Q1;
            Q1 = qSketchRegion(id + "F18", true);
            loft(context, id + "F19", {"operationType" : NewBodyOperationType.REMOVE, "sheetProfilesArray" : [{ "sheetProfileEntities" : qUnion([Q0]) }, { "sheetProfileEntities" : qUnion([Q1]) }]});
        }
        {
            var Q0;
            Q0=makeQuery(id+"F19.boolean.opBoolean","COPY",FACE,{"derivedFrom":makeQuery(id+"F19.opLoft","SWEPT_FACE",FACE,{"disambiguationData":[OSD([sQuery(id+"F16.wireOp",EDGE,"E233.0"),sQuery(id+"F16.wireOp",EDGE,"E233.2"),sQuery(id+"F16.wireOp",EDGE,"E233.3"),sQuery(id+"F18.wireOp",EDGE,"E234.0"),sQuery(id+"F18.wireOp",EDGE,"E234.1"),sQuery(id+"F18.wireOp",EDGE,"E234.2")])]})});
            extrude(context, id + "F20", {"entities" : qUnion([Q0]), "operationType" : NewBodyOperationType.REMOVE, "oppositeDirection" : true, "depth" : 25.4 * mm, "offsetDistance" : 25.4 * mm});
        }
        {
            var Q0;
            Q0=makeQuery(id+"F20.boolean.opBoolean","COPY",FACE,{"derivedFrom":makeQuery(id+"F20.opExtrude","SWEPT_FACE",FACE,{"disambiguationData":[OSD([sQuery(id+"F18.wireOp",EDGE,"E234.0"),sQuery(id+"F18.wireOp",EDGE,"E234.1"),sQuery(id+"F18.wireOp",EDGE,"E234.2")])]})});
            extrude(context, id + "F21", {"entities" : qUnion([Q0]), "operationType" : NewBodyOperationType.REMOVE, "oppositeDirection" : true, "depth" : 25.4 * mm, "offsetDistance" : 25.4 * mm});
        }
        {
            var Q0;
            {var subQ1=sQuery(id+"F13.wireOp",EDGE,"E223");Q0=makeQuery(id+"F13.imprint","IMPRINT",FACE,{"disambiguationData":[TD([[makeQuery(id+"F13.imprint","IMPRINT",EDGE,{"derivedFrom":subQ1}),-1.0]])]});}
            var sketch = newSketch(context, id + "F22", { "sketchPlane" : qUnion([Q0])});
            skLineSegment(sketch, "E236.bottom", {"start": v(3401.53, -732.75) * mm, "end": v(3320.88, -732.75) * mm});
            skLineSegment(sketch, "E236.top", {"start": v(3401.53, -813.4) * mm, "end": v(3320.88, -813.4) * mm});
            skLineSegment(sketch, "E236.left", {"start": v(3401.53, -732.75) * mm, "end": v(3401.53, -813.4) * mm});
            skLineSegment(sketch, "E236.right", {"start": v(3320.88, -732.75) * mm, "end": v(3320.88, -813.4) * mm});
            skSolve(sketch);
        }
        {
            var Q0;
            Q0=makeQuery(id+"F7.boolean.opBoolean","COPY",FACE,{"derivedFrom":makeQuery(id+"F7.opExtrude","SWEPT_FACE",FACE,{"disambiguationData":[OSD([sQuery(id+"F6.wireOp",EDGE,"E213.0.3.0")])]})});
            var sketch = newSketch(context, id + "F23", { "sketchPlane" : qUnion([Q0])});
            skLineSegment(sketch, "E237.bottom", {"start": v(1121.35, -155.13) * mm, "end": v(1202, -155.13) * mm});
            skLineSegment(sketch, "E237.top", {"start": v(1121.35, -235.78) * mm, "end": v(1202, -235.78) * mm});
            skLineSegment(sketch, "E237.left", {"start": v(1121.35, -155.13) * mm, "end": v(1121.35, -235.78) * mm});
            skLineSegment(sketch, "E237.right", {"start": v(1202, -155.13) * mm, "end": v(1202, -235.78) * mm});
            skSolve(sketch);
        }
        {
            var Q0;
            Q0 = qSketchRegion(id + "F23", true);
            var Q1;
            Q1 = qSketchRegion(id + "F22", true);
            loft(context, id + "F24", {"operationType" : NewBodyOperationType.REMOVE, "sheetProfilesArray" : [{ "sheetProfileEntities" : qUnion([Q0]) }, { "sheetProfileEntities" : qUnion([Q1]) }]});
        }
    });
